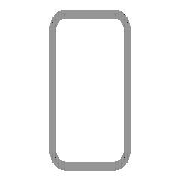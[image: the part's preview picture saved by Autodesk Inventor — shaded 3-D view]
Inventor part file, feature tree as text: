
AUTODESK INVENTOR PART (.ipt)
format: ipt  version: 2025 (Build 290162010, 162A)  size: 132,608 bytes
history: native  units: mm (DEFAULTED — no unit token found)
features: other x4, sketch x1, plane x1
ambient origin geometry x8: Origin, YZ Plane, XZ Plane, XY Plane, X Axis, Y Axis, Z Axis, Center Point
bodies: Solid1 (feature_tree), Body (feature_tree)
feature tree (6):
  parser-record x1  (decoder bookkeeping rows leaked as tree rows — omitted from the tree; the rows remain in map.json)
  other  "Driven Length"
  other  "Start Plane"
  other  "End Plane"
  sketch  "Sketch3"  dims[d3=600.0mm d4=0.0mm d7=8.0mm d9=50.0mm d11=100.0mm d12=4.0mm d13=-0.0mm d14=600.0mm d15=25.0mm d16=50.0mm d17=90.0deg d18=600.0mm]
  plane  "Work Plane3"
